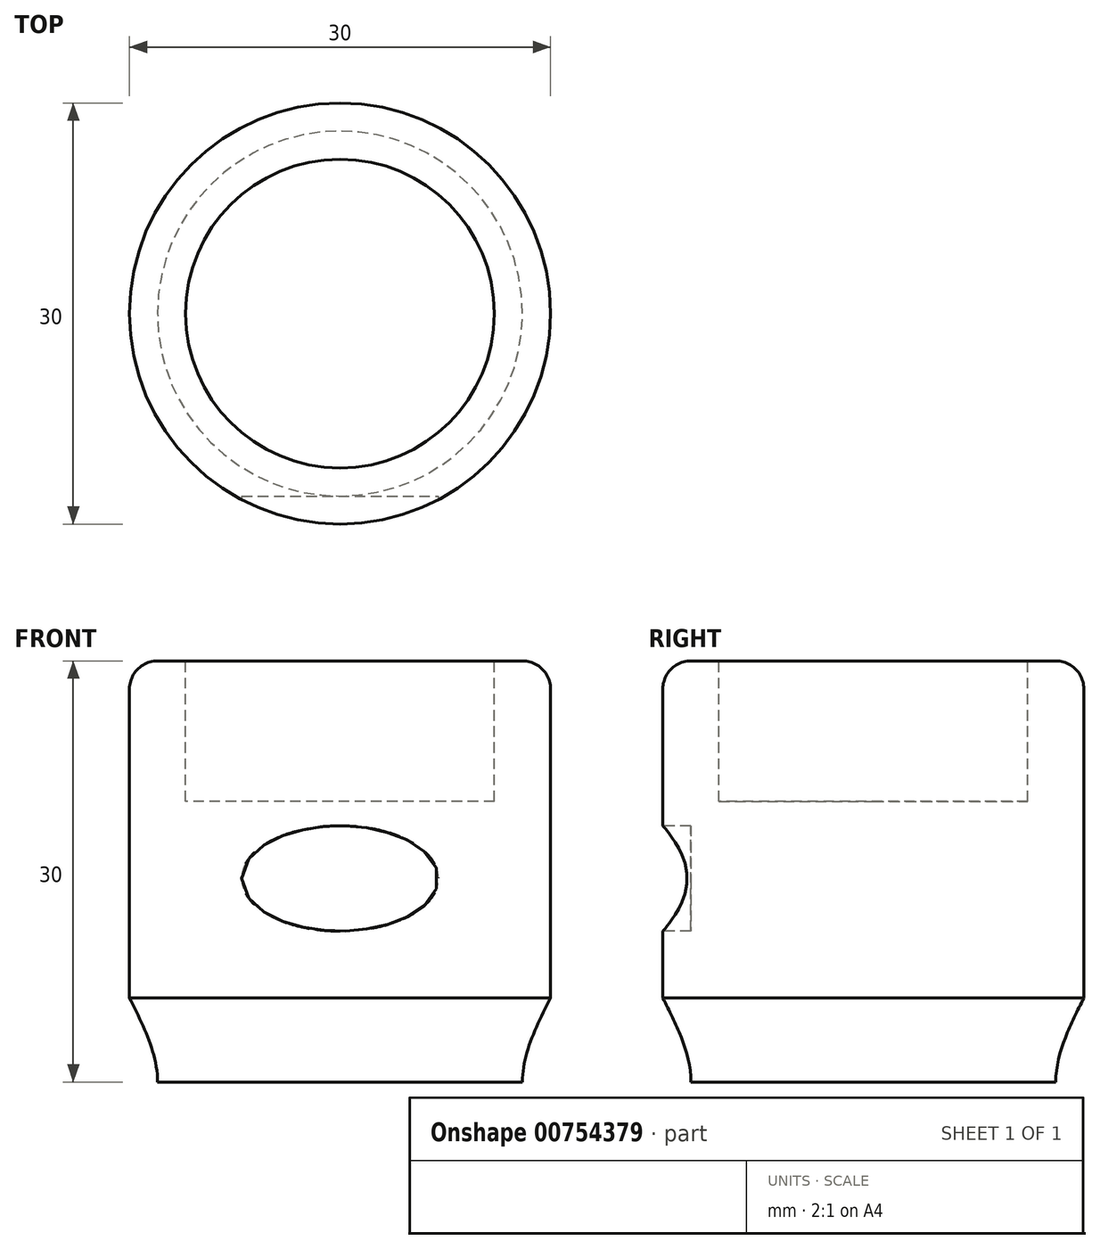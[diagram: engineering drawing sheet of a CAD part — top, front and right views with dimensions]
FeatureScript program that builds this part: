
annotation { "Feature Type Name" : "Feature", "Feature Type Description" : "" }
export const myFeature = defineFeature(function(context is Context, id is Id, definition is map)
    precondition{}
    {
        {
            var Q0;
            Q0=qCreatedBy(makeId("Top.planeOp"),FACE);
            var sketch = newSketch(context, id + "F0", { "sketchPlane" : qUnion([Q0])});
            skCircle(sketch, "E0", {"center": v(0, 0) * mm, "radius": 15 * mm});
            skSolve(sketch);
        }
        {
            var Q0;
            Q0=qCreatedBy(makeId("Top.planeOp"),FACE);
            cPlane(context, id + "F1", {"entities" : qUnion([Q0]), "cplaneType" : CPlaneType.OFFSET, "offset" : 6 * mm, "oppositeDirection" : true, "width" : 150 * mm, "height" : 150 * mm});
        }
        {
            var Q0;
            Q0=qCreatedBy(id+"F1.planeOp",FACE);
            var sketch = newSketch(context, id + "F2", { "sketchPlane" : qUnion([Q0])});
            skCircle(sketch, "E1", {"center": v(0, 0) * mm, "radius": 13 * mm});
            skSolve(sketch);
        }
        {
            var Q0;
            Q0=makeQuery(id+"F0.imprint","IMPRINT",FACE,{"disambiguationData":[TD([[makeQuery(id+"F0.imprint","IMPRINT",EDGE,{"derivedFrom":sQuery(id+"F0.wireOp",EDGE,"E0")}),1.0]])]});
            extrude(context, id + "F3", {"entities" : qUnion([Q0]), "depth" : 24 * mm, "offsetDistance" : 25 * mm});
        }
        {
            var Q1;
            Q1=makeQuery(id+"F3.opExtrude","CAP_FACE",FACE,{"disambiguationData":[OSD([sQuery(id+"F0.wireOp",EDGE,"E0")])],"isStart":true});
            var Q2;
            Q2=makeQuery(id+"F2.imprint","IMPRINT",FACE,{"disambiguationData":[TD([[makeQuery(id+"F2.imprint","IMPRINT",EDGE,{"derivedFrom":sQuery(id+"F2.wireOp",EDGE,"E1")}),1.0]])]});
            loft(context, id + "F4", {"operationType" : NewBodyOperationType.ADD, "endCondition" : LoftEndDerivativeType.NORMAL_TO_PROFILE, "endMagnitude" : 1, "sheetProfilesArray" : [{ "sheetProfileEntities" : qUnion([Q1]) }, { "sheetProfileEntities" : qUnion([Q2]) }]});
        }
        {
            var Q0;
            Q0=makeQuery(id+"F3.opExtrude","CAP_EDGE",EDGE,{"disambiguationData":[OSD([sQuery(id+"F0.wireOp",EDGE,"E0")])],"isStart":false});
            fillet(context, id + "F5", {"entities" : qUnion([Q0]), "radius" : 2 * mm, "tangentPropagation" : true, "allowEdgeOverflow" : false});
        }
        {
            var Q0;
            Q0=makeQuery(id+"F3.opExtrude","CAP_FACE",FACE,{"disambiguationData":[OSD([sQuery(id+"F0.wireOp",EDGE,"E0")])],"isStart":false});
            var sketch = newSketch(context, id + "F6", { "sketchPlane" : qUnion([Q0])});
            skCircle(sketch, "E2", {"center": v(0, 0) * mm, "radius": 11 * mm});
            skSolve(sketch);
        }
        {
            var Q0;
            Q0 = qSketchRegion(id + "F6", true);
            extrude(context, id + "F7", {"entities" : qUnion([Q0]), "operationType" : NewBodyOperationType.REMOVE, "oppositeDirection" : true, "depth" : 10 * mm, "offsetDistance" : 25 * mm});
        }
        {
            var Q0;
            Q0=qCreatedBy(makeId("Front.planeOp"),FACE);
            cPlane(context, id + "F8", {"entities" : qUnion([Q0]), "cplaneType" : CPlaneType.OFFSET, "offset" : 25 * mm, "width" : 150 * mm, "height" : 150 * mm});
        }
        {
            var Q0;
            Q0=qCreatedBy(id+"F8.planeOp",FACE);
            var sketch = newSketch(context, id + "F9", { "sketchPlane" : qUnion([Q0])});
            skLineSegment(sketch, "E3", {"start": v(0, 0) * mm, "end": v(0, 8.5) * mm});
            skEllipse(sketch, "E4", {"center": v(0, 8.5) * mm, "majorRadius": 7 * mm, "minorRadius": 3.75 * mm, "majorAxis": v(-1, 0)});
            skSolve(sketch);
        }
        {
            var Q0;
            Q0 = qSketchRegion(id + "F9", true);
            extrude(context, id + "F10", {"entities" : qUnion([Q0]), "operationType" : NewBodyOperationType.REMOVE, "oppositeDirection" : true, "depth" : 12 * mm, "offsetDistance" : 25 * mm});
        }
    });
